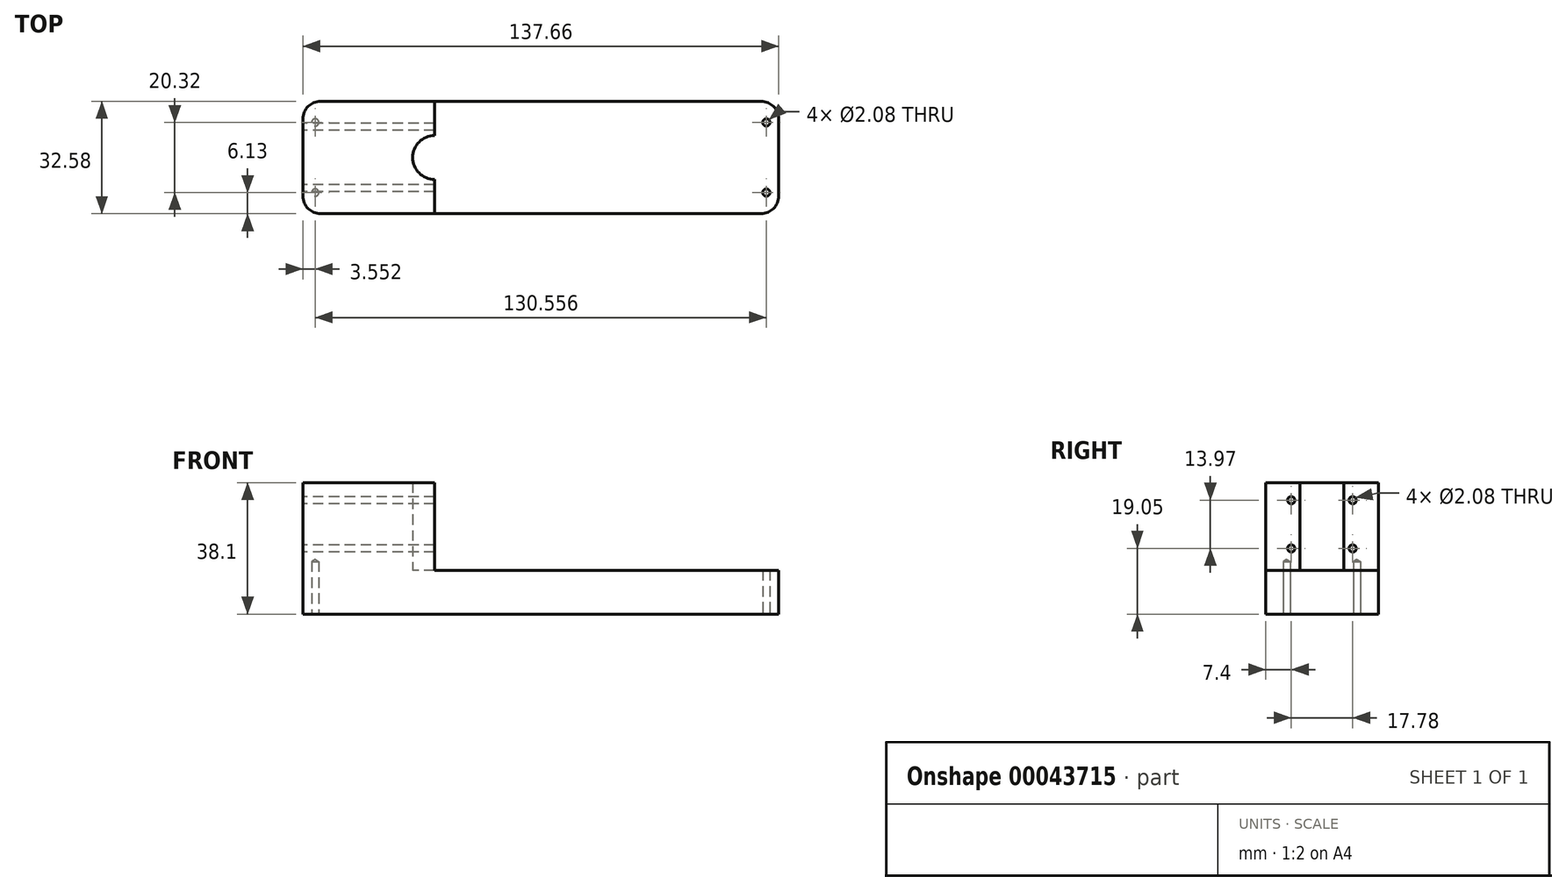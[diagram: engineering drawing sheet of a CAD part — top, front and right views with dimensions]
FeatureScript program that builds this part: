
annotation { "Feature Type Name" : "Feature", "Feature Type Description" : "" }
export const myFeature = defineFeature(function(context is Context, id is Id, definition is map)
    precondition{}
    {
        {
            var Q0;
            Q0=qCreatedBy(makeId("Top.planeOp"),FACE);
            var sketch = newSketch(context, id + "F0", { "sketchPlane" : qUnion([Q0])});
            skLineSegment(sketch, "E0.rect.bottom", {"start": v(-63.75, -16.3) * mm, "end": v(63.75, -16.3) * mm});
            skLineSegment(sketch, "E0.rect.top", {"start": v(-63.75, 16.3) * mm, "end": v(63.75, 16.3) * mm});
            skLineSegment(sketch, "E0.rect.left", {"start": v(-68.83, -11.21) * mm, "end": v(-68.83, 11.21) * mm});
            skLineSegment(sketch, "E0.rect.right", {"start": v(68.83, -11.21) * mm, "end": v(68.83, 11.21) * mm});
            skPoint(sketch, "E0.rect.middle", {"position": v(0, 0) * mm});
            skLineSegment(sketch, "E1.rect.bottom", {"start": v(-65.28, -10.16) * mm, "end": v(65.28, -10.16) * mm, "construction": true});
            skLineSegment(sketch, "E1.rect.top", {"start": v(-65.28, 10.16) * mm, "end": v(65.28, 10.16) * mm, "construction": true});
            skLineSegment(sketch, "E1.rect.left", {"start": v(-65.28, -10.16) * mm, "end": v(-65.28, 10.16) * mm, "construction": true});
            skLineSegment(sketch, "E1.rect.right", {"start": v(65.28, -10.16) * mm, "end": v(65.28, 10.16) * mm, "construction": true});
            skPoint(sketch, "E2.visualSharp", {"position": v(-68.83, 16.3) * mm});
            skArc(sketch, "E2.filletArc", {"start": v(-63.75, 16.3) * mm, "mid": v(-67.35, 14.8) * mm, "end": v(-68.83, 11.21) * mm});
            skPoint(sketch, "E3.visualSharp", {"position": v(-68.83, -16.3) * mm});
            skArc(sketch, "E3.filletArc", {"start": v(-68.83, -11.21) * mm, "mid": v(-67.35, -14.8) * mm, "end": v(-63.75, -16.3) * mm});
            skPoint(sketch, "E4.visualSharp", {"position": v(68.83, 16.3) * mm});
            skArc(sketch, "E4.filletArc", {"start": v(68.83, 11.21) * mm, "mid": v(67.35, 14.8) * mm, "end": v(63.75, 16.3) * mm});
            skPoint(sketch, "E5.visualSharp", {"position": v(68.83, -16.3) * mm});
            skArc(sketch, "E5.filletArc", {"start": v(63.75, -16.3) * mm, "mid": v(67.35, -14.8) * mm, "end": v(68.83, -11.21) * mm});
            skCircle(sketch, "E6", {"center": v(65.28, -10.16) * mm, "radius": 1.04 * mm});
            skCircle(sketch, "E7", {"center": v(65.28, 10.16) * mm, "radius": 1.04 * mm});
            skSolve(sketch);
        }
        {
            var Q0;
            Q0=makeQuery(id+"F0.imprint","IMPRINT",FACE,{"disambiguationData":[TD([[makeQuery(id+"F0.imprint","IMPRINT",EDGE,{"derivedFrom":sQuery(id+"F0.wireOp",EDGE,"E0.rect.bottom")}),1.0]])]});
            extrude(context, id + "F1", {"entities" : qUnion([Q0]), "depth" : 12.7 * mm});
        }
        {
            var Q0;
            Q0=makeQuery(id+"F1.opExtrude","CAP_FACE",FACE,{"disambiguationData":[OSD([sQuery(id+"F0.wireOp",EDGE,"E0.rect.bottom"),sQuery(id+"F0.wireOp",EDGE,"E0.rect.top"),sQuery(id+"F0.wireOp",EDGE,"E0.rect.left"),sQuery(id+"F0.wireOp",EDGE,"E0.rect.right"),sQuery(id+"F0.wireOp",EDGE,"246df52f-a14a-4190-a2f5-bf559bc65bf0"),sQuery(id+"F0.wireOp",EDGE,"b3b8decf-7409-4ac1-8fde-c912ab8a51f7"),sQuery(id+"F0.wireOp",EDGE,"E2.filletArc"),sQuery(id+"F0.wireOp",EDGE,"E3.filletArc")])],"isStart":false});
            var sketch = newSketch(context, id + "F2", { "sketchPlane" : qUnion([Q0])});
            skLineSegment(sketch, "E8.bottom", {"start": v(-63.75, 16.3) * mm, "end": v(-30.73, 16.3) * mm});
            skLineSegment(sketch, "E8.top", {"start": v(-63.75, -16.3) * mm, "end": v(-30.73, -16.3) * mm});
            skLineSegment(sketch, "E8.left", {"start": v(-68.83, 11.21) * mm, "end": v(-68.83, -11.21) * mm});
            skLineSegment(sketch, "E8.right", {"start": v(-30.73, 16.3) * mm, "end": v(-30.73, 6.35) * mm});
            skPoint(sketch, "E9.visualSharp", {"position": v(-68.83, 16.3) * mm});
            skArc(sketch, "E9.filletArc", {"start": v(-63.75, 16.3) * mm, "mid": v(-67.35, 14.8) * mm, "end": v(-68.83, 11.21) * mm});
            skPoint(sketch, "E10.visualSharp", {"position": v(-68.83, -16.3) * mm});
            skArc(sketch, "E10.filletArc", {"start": v(-68.83, -11.21) * mm, "mid": v(-67.35, -14.8) * mm, "end": v(-63.75, -16.3) * mm});
            skLineSegment(sketch, "E11", {"start": v(-68.83, 0) * mm, "end": v(-30.73, 0) * mm, "construction": true});
            skArc(sketch, "E12", {"start": v(-30.73, 6.35) * mm, "mid": v(-37.08, 0) * mm, "end": v(-30.73, -6.35) * mm});
            skLineSegment(sketch, "E13.trimOffspring", {"start": v(-30.73, -6.35) * mm, "end": v(-30.73, -16.3) * mm});
            skSolve(sketch);
        }
        {
            var Q0;
            Q0=makeQuery(id+"F2.imprint","IMPRINT",FACE,{"disambiguationData":[TD([[makeQuery(id+"F2.imprint","IMPRINT",EDGE,{"derivedFrom":sQuery(id+"F2.wireOp",EDGE,"E8.bottom")}),-1.0]])]});
            extrude(context, id + "F3", {"entities" : qUnion([Q0]), "operationType" : NewBodyOperationType.ADD, "depth" : 25.4 * mm});
        }
        {
            var Q0;
            Q0=makeQuery(id+"F3.boolean.opBoolean","MERGE",FACE,{"derivedFrom":[makeQuery(id+"F1.opExtrude","SWEPT_FACE",FACE,{"disambiguationData":[OSD([sQuery(id+"F0.wireOp",EDGE,"E0.rect.left")])]}),makeQuery(id+"F3.opExtrude","SWEPT_FACE",FACE,{"disambiguationData":[OSD([sQuery(id+"F2.wireOp",EDGE,"E8.left")])]})]});
            var sketch = newSketch(context, id + "F4", { "sketchPlane" : qUnion([Q0])});
            skLineSegment(sketch, "E14", {"start": v(0, 38.1) * mm, "end": v(0, 0) * mm, "construction": true});
            skLineSegment(sketch, "E15", {"start": v(-11.21, 19.05) * mm, "end": v(11.21, 19.05) * mm, "construction": true});
            skLineSegment(sketch, "E16.MirrorCS", {"start": v(0, 0) * mm, "end": v(0, 38.1) * mm, "construction": true});
            skCircle(sketch, "E17", {"center": v(-8.9, 33.02) * mm, "radius": 1.04 * mm});
            skCircle(sketch, "E18.MirrorC", {"center": v(8.89, 33.02) * mm, "radius": 1.04 * mm});
            skLineSegment(sketch, "E19", {"start": v(-8.9, 33.02) * mm, "end": v(-8.9, 0) * mm, "construction": true});
            skLineSegment(sketch, "E20", {"start": v(8.89, 33.02) * mm, "end": v(8.89, 0) * mm, "construction": true});
            skCircle(sketch, "E21", {"center": v(-8.9, 19.05) * mm, "radius": 1.04 * mm});
            skCircle(sketch, "E22.MirrorC", {"center": v(8.89, 19.05) * mm, "radius": 1.04 * mm});
            skSolve(sketch);
        }
        {
            var Q0;
            Q0=sQuery(id+"F4.wireOp",VERTEX,"E17.center");
            var Q1;
            Q1=sQuery(id+"F4.wireOp",VERTEX,"E21.center");
            var Q2;
            Q2=sQuery(id+"F4.wireOp",VERTEX,"E18.MirrorC.center");
            var Q3;
            Q3=sQuery(id+"F4.wireOp",VERTEX,"E22.MirrorC.center");
            var Q4;
            Q4=makeQuery(id+"F1.opExtrude","SWEPT_BODY",BODY,{"disambiguationData":[OSD([sQuery(id+"F0.wireOp",EDGE,"E0.rect.bottom"),sQuery(id+"F0.wireOp",EDGE,"E0.rect.top"),sQuery(id+"F0.wireOp",EDGE,"E0.rect.left"),sQuery(id+"F0.wireOp",EDGE,"E0.rect.right"),sQuery(id+"F0.wireOp",EDGE,"246df52f-a14a-4190-a2f5-bf559bc65bf0"),sQuery(id+"F0.wireOp",EDGE,"b3b8decf-7409-4ac1-8fde-c912ab8a51f7"),sQuery(id+"F0.wireOp",EDGE,"E2.filletArc"),sQuery(id+"F0.wireOp",EDGE,"E3.filletArc"),sQuery(id+"F0.wireOp",EDGE,"E4.filletArc"),sQuery(id+"F0.wireOp",EDGE,"E5.filletArc")])]});
            hole(context, id + "F5", {"style" : HoleStyle.SIMPLE, "holeDiameter" : 2.08 * mm, "endStyle" : HoleEndStyle.THROUGH, "locations" : qUnion([Q0, Q1, Q2, Q3]), "scope" : qUnion([Q4])});
        }
        {
            var Q0;
            Q0=makeQuery(id+"F1.opExtrude","CAP_FACE",FACE,{"disambiguationData":[OSD([sQuery(id+"F0.wireOp",EDGE,"E0.rect.bottom"),sQuery(id+"F0.wireOp",EDGE,"E0.rect.top"),sQuery(id+"F0.wireOp",EDGE,"E0.rect.left"),sQuery(id+"F0.wireOp",EDGE,"E0.rect.right"),sQuery(id+"F0.wireOp",EDGE,"E2.filletArc"),sQuery(id+"F0.wireOp",EDGE,"E3.filletArc"),sQuery(id+"F0.wireOp",EDGE,"E4.filletArc"),sQuery(id+"F0.wireOp",EDGE,"E5.filletArc"),sQuery(id+"F0.wireOp",EDGE,"E6"),sQuery(id+"F0.wireOp",EDGE,"E7")])],"isStart":true});
            var sketch = newSketch(context, id + "F6", { "sketchPlane" : qUnion([Q0])});
            skLineSegment(sketch, "E23", {"start": v(-68.83, 0) * mm, "end": v(-30.05, 0) * mm, "construction": true});
            skCircle(sketch, "E24", {"center": v(-65.28, 10.16) * mm, "radius": 1.04 * mm});
            skCircle(sketch, "E25.MirrorC", {"center": v(-65.28, -10.16) * mm, "radius": 1.04 * mm});
            skSolve(sketch);
        }
        {
            var Q0;
            Q0=sQuery(id+"F6.wireOp",VERTEX,"E24.center");
            var Q1;
            Q1=sQuery(id+"F6.wireOp",VERTEX,"E25.MirrorC.center");
            var Q2;
            Q2=makeQuery(id+"F1.opExtrude","SWEPT_BODY",BODY,{"disambiguationData":[OSD([sQuery(id+"F0.wireOp",EDGE,"E0.rect.bottom"),sQuery(id+"F0.wireOp",EDGE,"E0.rect.top"),sQuery(id+"F0.wireOp",EDGE,"E0.rect.left"),sQuery(id+"F0.wireOp",EDGE,"E0.rect.right"),sQuery(id+"F0.wireOp",EDGE,"E2.filletArc"),sQuery(id+"F0.wireOp",EDGE,"E3.filletArc"),sQuery(id+"F0.wireOp",EDGE,"E4.filletArc"),sQuery(id+"F0.wireOp",EDGE,"E5.filletArc"),sQuery(id+"F0.wireOp",EDGE,"E6"),sQuery(id+"F0.wireOp",EDGE,"E7")])]});
            hole(context, id + "F7", {"style" : HoleStyle.SIMPLE, "holeDiameter" : 2.08 * mm, "endStyle" : HoleEndStyle.BLIND, "holeDepth" : 15.24 * mm, "locations" : qUnion([Q0, Q1]), "scope" : qUnion([Q2])});
        }
    });
